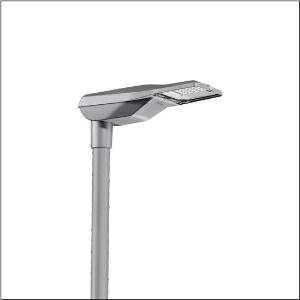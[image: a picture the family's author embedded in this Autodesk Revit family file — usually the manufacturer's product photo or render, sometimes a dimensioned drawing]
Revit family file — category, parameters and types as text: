
# Revit family: streetlight_sl_21_iq_micro___st1_0a_5xe1d31d08db_2abd
name_source: partatom
category: Lighting Fixtures
units: mm (PartAtom-declared; Revit-internal decimal feet)

## family parameters
Cut with Voids When Loaded = No
Host = Face
Light Source = No
Part Type = Normal
Room Calculation Point = No
Round Connector Dimension = Use Diameter
Shared = No

## types (1)
- --- (1 x LED, 4810 lm, 36.4 W, 3000K)
    Apparent Load = 36 VA
    CIE Flux Codes = 37 72 97 100 100
    Color Rendering = 70
    Color Temperature = 3000K
    Default Elevation = 1800 mm
    Description = Streetlight SL 21 iQ micro, mast luminaire, primary light control with lens, of PMMA, primary optical cover: cover, of toughened safety glass, transparent, light distribution: ST1.0a, light emission: direct distribution, primary light characteristic: asymmetric, installation type: post-top, side-entry, LED, High Power LED, rated luminous flux: 4.810lm, luminous efficacy: 132lm/W, light colour: 730, colour temperature: 3000K, control: Auto-Match, Temp-Guard, Lumen-Switch, Night-Set, Smart-Wire, Light-Fading, Desk-Remote (wireless, voltage-free reading and setting of iQ features in the workshop via application-optimized NFC function/RFID function), optimised constant luminous flux control (CLO 2.0), presetting dimming linear, mains connection: 220..240V, AC, 50/60Hz, start of lifetime: 36W, end of service life: 38W, reduction: 16W, luminaire housing, of diecast aluminium, powder-coated, Siteco® metallic grey (DB 702S), corrosivity category C5 mid according to DIN EN ISO 12944, please order mast flange separately, inclination adjustable: 0°, 5°, 10°, 15°, sealing non-destructively replaceable, multi-level sealing system, length: 528mm, width: 235mm, height: 110mm, mast flange for spigot size: 42mm (side-entry): 5XC10008XM4, 60/48mm (side-entry/post-top): 5XC10108XM2, 76/60mm (side-entry/post-top): 5XC10108XM1, protection rating (complete): IP66, insulation class (complete): insulation class II (safety insulation), certification: CE, ENEC, ENEC+, VDE, impact resistance: IK09, permissible operating ambient temperature for outdoor applications: -40..+50°C, standard-compliant lighting for roads and squares, packaging unit: 1 piece

Light Distribution: ST1.0a
    Height = 110 mm
    Lamp = 1 x LED
    Lamp Light Flux = 4810 lm
    Lamp Power = 36.4 W
    Lamp count = 1
    Length = 528 mm
    Luminous efficacy = 132 lm/W
    Manufacturer = Siteco
    ModVariant = No
    Model = 5XE1D31D08DB
    Number of Poles = 1
    OnlyDefault = Yes
    Power Factor = 1
    Product Name = Streetlight SL 21 iQ micro | ST1.0a
    Product group = mast luminaire | pylon top
    ProductGroupID = 6100
    Protection Class = Protection class II
    Protection Degree = IP 66
    RLX_Detail_Level = 1
    RLX_Emergency_Light_Flux = 0 lm
    RLX_Emergency_Type = 0
    RLX_Emergency_Type_DB = No
    RlxData = <blob elided: 99201 chars, md5=0c7122b3>
    Socket = socket
    Standby Power = 0 W
    System Light Flux = 4810 lm
    System Power = 36 W
    Type Comments = factory setting: luminous flux: 100 % | dim-lin: 254 | 715 mA
    Type Image = l_1006881.jpg
    URL = http://relux.com
    VarID = @adj_106181
    Voltage = 0 V
    Weight = 0.00 kg
    Width = 235 mm

## geometry (parser evidence)
native form markers: Blend x4, Sweep x10
no freeform markers — native parametric forms only
